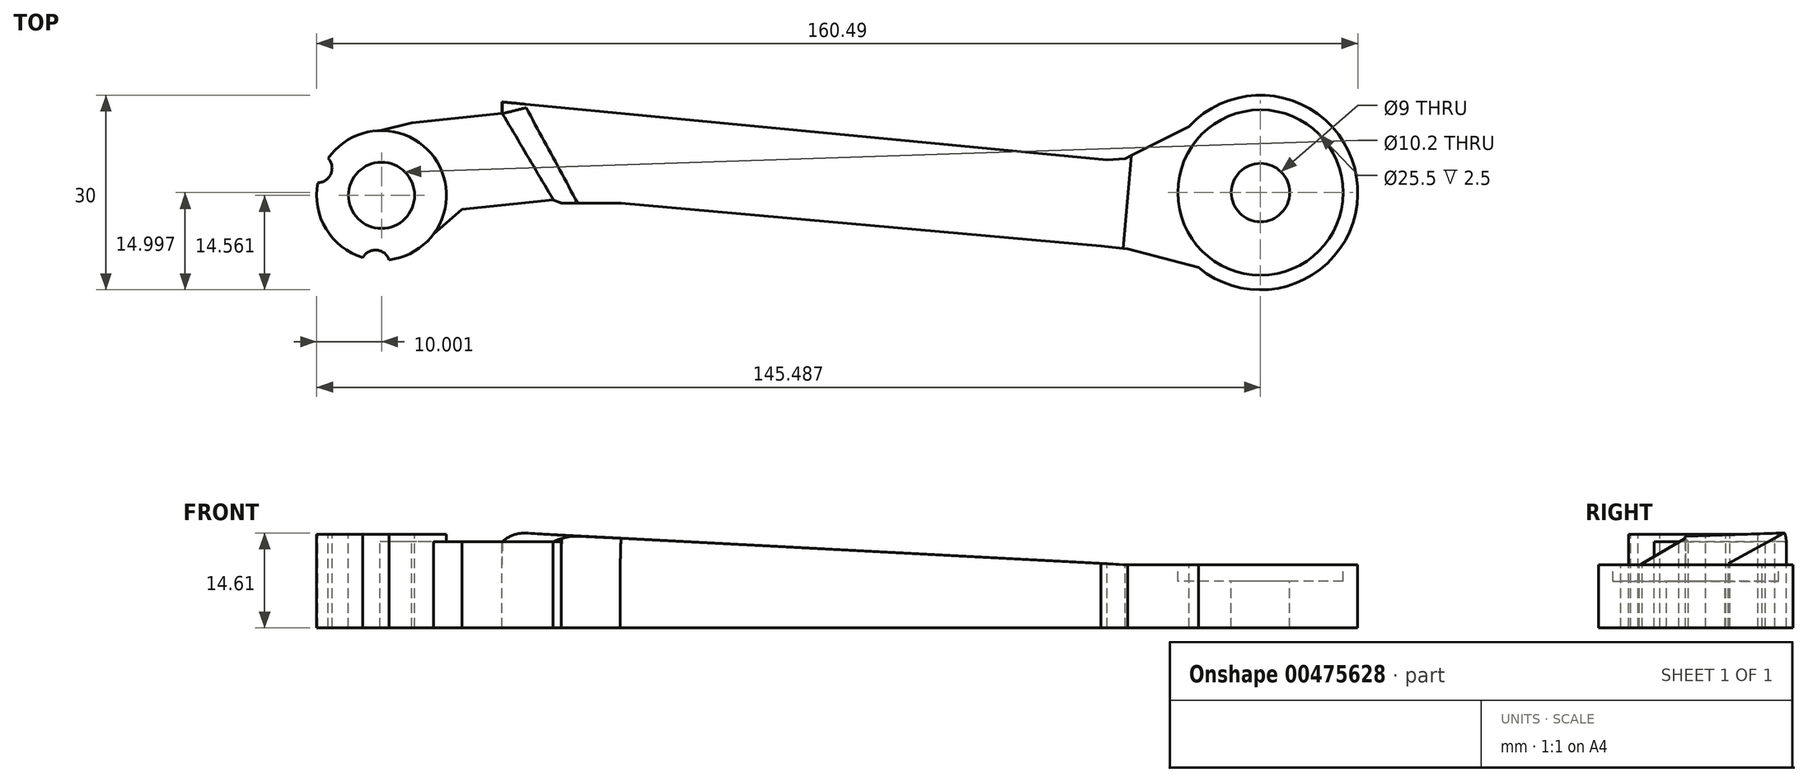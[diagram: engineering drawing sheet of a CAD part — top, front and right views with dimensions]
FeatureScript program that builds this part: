
annotation { "Feature Type Name" : "Feature", "Feature Type Description" : "" }
export const myFeature = defineFeature(function(context is Context, id is Id, definition is map)
    precondition{}
    {
        {
            var Q0;
            Q0=qCreatedBy(makeId("Top.planeOp"),FACE);
            var sketch = newSketch(context, id + "F0", { "sketchPlane" : qUnion([Q0])});
            skCircle(sketch, "E0", {"center": v(-70.2, 20.02) * mm, "radius": 5.1 * mm});
            skCircle(sketch, "E1", {"center": v(-70.2, 20.02) * mm, "radius": 10 * mm});
            skCircle(sketch, "E2", {"center": v(65.28, 20.46) * mm, "radius": 4.5 * mm});
            skCircle(sketch, "E3", {"center": v(65.28, 20.46) * mm, "radius": 12.75 * mm});
            skLineSegment(sketch, "E4", {"start": v(-51.63, 34.43) * mm, "end": v(41.63, 25.47) * mm});
            skLineSegment(sketch, "E5", {"start": v(-42.53, 18.85) * mm, "end": v(-33.4, 18.85) * mm});
            skLineSegment(sketch, "E6", {"start": v(-33.4, 18.85) * mm, "end": v(40.68, 12.22) * mm});
            skLineSegment(sketch, "E7", {"start": v(40.68, 12.22) * mm, "end": v(44.78, 11.78) * mm});
            skLineSegment(sketch, "E8", {"start": v(41.63, 25.47) * mm, "end": v(44.44, 25.7) * mm});
            skCircle(sketch, "E9", {"center": v(65.28, 20.46) * mm, "radius": 15 * mm});
            skLineSegment(sketch, "E10", {"start": v(44.78, 11.78) * mm, "end": v(55.72, 8.9) * mm});
            skLineSegment(sketch, "E11", {"start": v(44.44, 25.7) * mm, "end": v(54.28, 30.66) * mm});
            skLineSegment(sketch, "E12", {"start": v(-51.63, 34.43) * mm, "end": v(-51.63, 32.64) * mm});
            skLineSegment(sketch, "E13", {"start": v(-51.63, 32.64) * mm, "end": v(-65.55, 31.21) * mm});
            skLineSegment(sketch, "E14", {"start": v(-65.55, 31.21) * mm, "end": v(-70.46, 30.02) * mm});
            skLineSegment(sketch, "E15", {"start": v(-42.53, 18.85) * mm, "end": v(-43.78, 19.3) * mm});
            skLineSegment(sketch, "E16", {"start": v(-43.78, 19.3) * mm, "end": v(-57.8, 17.87) * mm});
            skLineSegment(sketch, "E17", {"start": v(-57.8, 17.87) * mm, "end": v(-62.2, 14.05) * mm});
            skCircle(sketch, "E18", {"center": v(-71.14, 9.33) * mm, "radius": 2.25 * mm});
            skCircle(sketch, "E19", {"center": v(-80.09, 24.21) * mm, "radius": 2.25 * mm});
            skLineSegment(sketch, "E20", {"start": v(-80.09, 24.21) * mm, "end": v(-70.2, 20.02) * mm, "construction": true});
            skLineSegment(sketch, "E21", {"start": v(-70.2, 20.02) * mm, "end": v(-71.14, 9.33) * mm, "construction": true});
            skLineSegment(sketch, "E22", {"start": v(-51.63, 34.43) * mm, "end": v(-42.53, 18.85) * mm});
            skLineSegment(sketch, "E23", {"start": v(-51.63, 32.64) * mm, "end": v(-43.78, 19.3) * mm});
            skLineSegment(sketch, "E24", {"start": v(36.26, 19.8) * mm, "end": v(-59.92, 28.22) * mm, "construction": true});
            skLineSegment(sketch, "E25", {"start": v(46.09, 34.45) * mm, "end": v(43.53, 5.16) * mm, "construction": true});
            skLineSegment(sketch, "E26", {"start": v(36.26, 19.8) * mm, "end": v(51.82, 18.44) * mm, "construction": true});
            skLineSegment(sketch, "E27.0", {"start": v(53.38, 20.08) * mm, "end": v(54.41, 31.95) * mm, "construction": true});
            skPoint(sketch, "E28", {"position": v(44.8, 19.8) * mm});
            skLineSegment(sketch, "E29", {"start": v(45.36, 26.17) * mm, "end": v(44.1, 11.78) * mm});
            skSolve(sketch);
        }
        {
            var Q0;
            Q0=makeQuery(id+"F0.imprint","IMPRINT",FACE,{"disambiguationData":[TD([[makeQuery(id+"F0.imprint","IMPRINT",EDGE,{"derivedFrom":sQuery(id+"F0.wireOp",EDGE,"E4")}),-1.0]])]});
            var Q1;
            Q1=makeQuery(id+"F0.imprint","IMPRINT",FACE,{"disambiguationData":[TD([[makeQuery(id+"F0.imprint","IMPRINT",EDGE,{"derivedFrom":sQuery(id+"F0.wireOp",EDGE,"E3")}),-1.0]])]});
            var Q2;
            Q2=makeQuery(id+"F0.imprint","IMPRINT",FACE,{"disambiguationData":[TD([[makeQuery(id+"F0.imprint","IMPRINT",EDGE,{"derivedFrom":sQuery(id+"F0.wireOp",EDGE,"E2")}),-1.0]])]});
            var Q3;
            Q3=makeQuery(id+"F0.imprint","IMPRINT",FACE,{"disambiguationData":[TD([[makeQuery(id+"F0.imprint","IMPRINT",EDGE,{"derivedFrom":sQuery(id+"F0.wireOp",EDGE,"E13")}),1.0]])]});
            var Q4;
            Q4=makeQuery(id+"F0.imprint","IMPRINT",FACE,{"disambiguationData":[TD([[makeQuery(id+"F0.imprint","IMPRINT",EDGE,{"derivedFrom":sQuery(id+"F0.wireOp",EDGE,"E0")}),-1.0]])]});
            var Q5;
            Q5=makeQuery(id+"F0.imprint","IMPRINT",FACE,{"disambiguationData":[TD([[makeQuery(id+"F0.imprint","IMPRINT",EDGE,{"derivedFrom":sQuery(id+"F0.wireOp",EDGE,"E12")}),1.0]])]});
            var Q6;
            {var subQ5=sQuery(id+"F0.wireOp",EDGE,"E10");Q6=makeQuery(id+"F0.imprint","IMPRINT",FACE,{"disambiguationData":[TD([[makeQuery(id+"F0.imprint","IMPRINT",EDGE,{"derivedFrom":subQ5}),1.0]])]});}
            extrude(context, id + "F1", {"entities" : qUnion([Q0, Q1, Q2, Q3, Q4, Q5, Q6]), "oppositeDirection" : true, "depth" : 9.7 * mm, "offsetDistance" : 25 * mm});
        }
        {
            var Q0;
            Q0=makeQuery(id+"F0.imprint","IMPRINT",FACE,{"disambiguationData":[TD([[makeQuery(id+"F0.imprint","IMPRINT",EDGE,{"derivedFrom":sQuery(id+"F0.wireOp",EDGE,"E2")}),-1.0]])]});
            extrude(context, id + "F2", {"entities" : qUnion([Q0]), "operationType" : NewBodyOperationType.REMOVE, "oppositeDirection" : true, "depth" : 2.5 * mm, "offsetDistance" : 25 * mm});
        }
        {
            var Q0;
            Q0=makeQuery(id+"F0.imprint","IMPRINT",FACE,{"disambiguationData":[TD([[makeQuery(id+"F0.imprint","IMPRINT",EDGE,{"derivedFrom":sQuery(id+"F0.wireOp",EDGE,"E4")}),-1.0]])]});
            var Q1;
            Q1=makeQuery(id+"F0.imprint","IMPRINT",FACE,{"disambiguationData":[TD([[makeQuery(id+"F0.imprint","IMPRINT",EDGE,{"derivedFrom":sQuery(id+"F0.wireOp",EDGE,"E12")}),1.0]])]});
            var Q2;
            Q2=sQuery(id+"F0.wireOp",EDGE,"E25");
            revolve(context, id + "F3", {"operationType" : NewBodyOperationType.ADD, "entities" : qUnion([Q0, Q1]), "axis" : qUnion([Q2]), "revolveType" : RevolveType.ONE_DIRECTION, "oppositeDirection" : true, "angle" : 3 * degree});
        }
        {
            var Q0;
            Q0=makeQuery(id+"F0.imprint","IMPRINT",FACE,{"disambiguationData":[TD([[makeQuery(id+"F0.imprint","IMPRINT",EDGE,{"derivedFrom":sQuery(id+"F0.wireOp",EDGE,"E13")}),1.0]])]});
            var Q1;
            Q1=makeQuery(id+"F0.imprint","IMPRINT",FACE,{"disambiguationData":[TD([[makeQuery(id+"F0.imprint","IMPRINT",EDGE,{"derivedFrom":sQuery(id+"F0.wireOp",EDGE,"E12")}),1.0]])]});
            extrude(context, id + "F4", {"entities" : qUnion([Q0, Q1]), "operationType" : NewBodyOperationType.ADD, "depth" : 3.6 * mm, "offsetDistance" : 25 * mm});
        }
        {
            var Q0;
            Q0=makeQuery(id+"F0.imprint","IMPRINT",FACE,{"disambiguationData":[TD([[makeQuery(id+"F0.imprint","IMPRINT",EDGE,{"derivedFrom":sQuery(id+"F0.wireOp",EDGE,"E0")}),-1.0]])]});
            extrude(context, id + "F5", {"entities" : qUnion([Q0]), "operationType" : NewBodyOperationType.ADD, "depth" : 4.7 * mm, "offsetDistance" : 25 * mm});
        }
        {
            var Q0;
            Q0=makeQuery(id+"F3.opRevolve","CAP_EDGE",EDGE,{"disambiguationData":[OSD([sQuery(id+"F0.wireOp",EDGE,"E23")])],"isStart":false});
            var Q1;
            Q1=makeQuery(id+"F3.opRevolve","CAP_EDGE",EDGE,{"disambiguationData":[OSD([sQuery(id+"F0.wireOp",EDGE,"E12")])],"isStart":false});
            fillet(context, id + "F6", {"entities" : qUnion([Q0, Q1]), "radius" : 5 * mm, "tangentPropagation" : true, "allowEdgeOverflow" : false});
        }
    });
